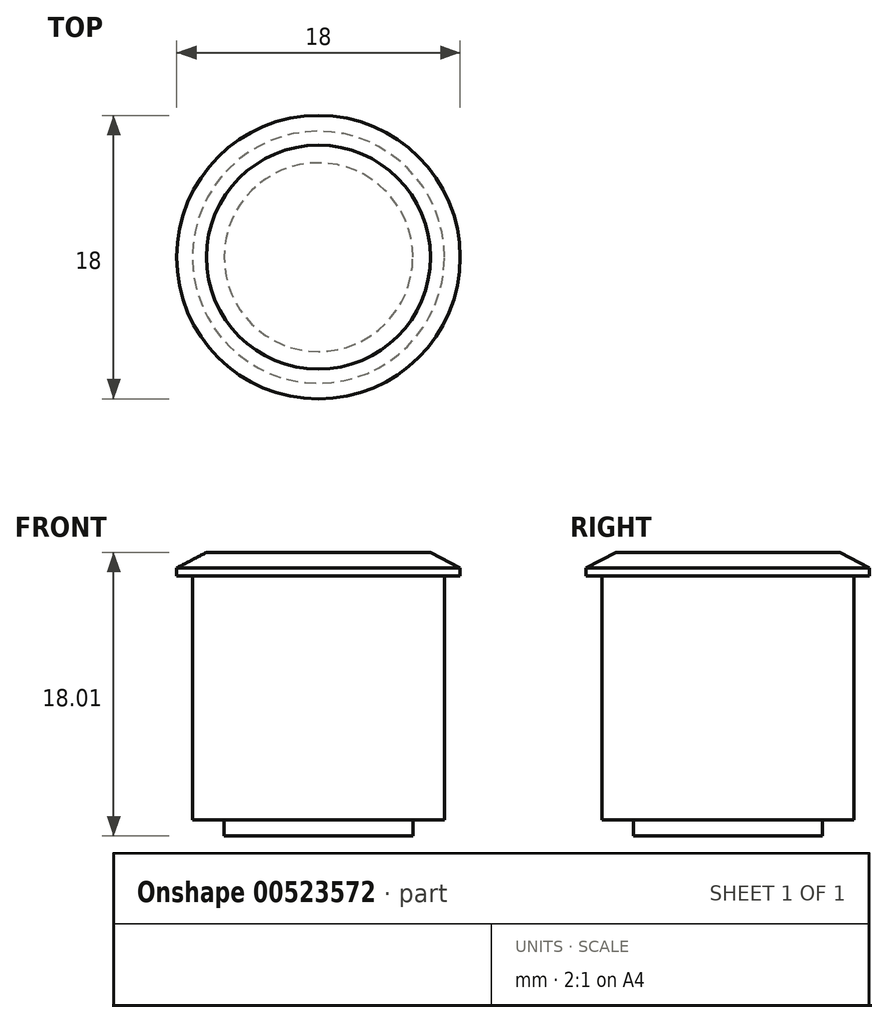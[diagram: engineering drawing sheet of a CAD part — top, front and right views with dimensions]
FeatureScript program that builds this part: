
annotation { "Feature Type Name" : "Feature", "Feature Type Description" : "" }
export const myFeature = defineFeature(function(context is Context, id is Id, definition is map)
    precondition{}
    {
        {
            var Q0;
            Q0=qCreatedBy(makeId("Front.planeOp"),FACE);
            var sketch = newSketch(context, id + "F0", { "sketchPlane" : qUnion([Q0])});
            skLineSegment(sketch, "E0", {"start": v(9, 0) * mm, "end": v(9, -0.5) * mm});
            skLineSegment(sketch, "E1", {"start": v(9, -0.5) * mm, "end": v(8, -0.5) * mm});
            skLineSegment(sketch, "E2", {"start": v(8, -0.5) * mm, "end": v(8, -16) * mm});
            skLineSegment(sketch, "E3", {"start": v(8, -16) * mm, "end": v(6, -16) * mm});
            skLineSegment(sketch, "E4", {"start": v(6, -16) * mm, "end": v(6, -17.02) * mm});
            skLineSegment(sketch, "E5", {"start": v(6, -17.02) * mm, "end": v(0, -17.02) * mm});
            skLineSegment(sketch, "E6", {"start": v(0, -17.02) * mm, "end": v(0, 0) * mm});
            skLineSegment(sketch, "E7", {"start": v(0, 0) * mm, "end": v(0, 1) * mm});
            skLineSegment(sketch, "E8", {"start": v(0, 1) * mm, "end": v(7.11, 1) * mm});
            skLineSegment(sketch, "E9", {"start": v(7.11, 1) * mm, "end": v(9, 0) * mm});
            skSolve(sketch);
        }
        {
            var Q0;
            Q0=makeQuery(id+"F0.imprint","IMPRINT",FACE,{"disambiguationData":[TD([[makeQuery(id+"F0.imprint","IMPRINT",EDGE,{"derivedFrom":sQuery(id+"F0.wireOp",EDGE,"E0")}),-1.0]])]});
            var Q1;
            Q1=sQuery(id+"F0.wireOp",EDGE,"E6");
            revolve(context, id + "F1", {"entities" : qUnion([Q0]), "axis" : qUnion([Q1]), "revolveType" : RevolveType.FULL});
        }
    });
